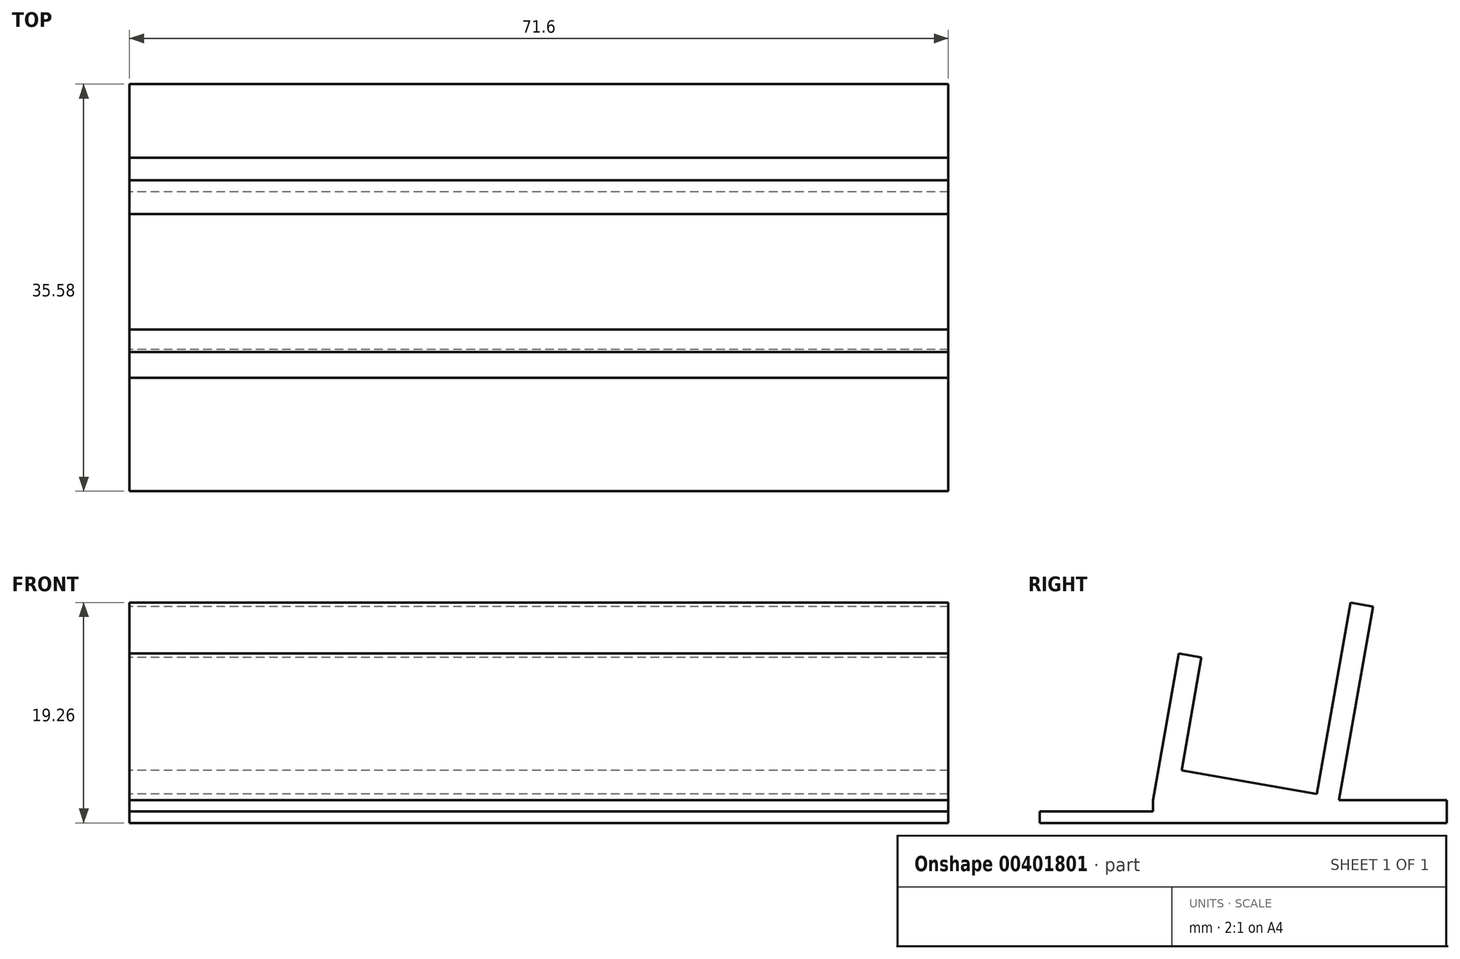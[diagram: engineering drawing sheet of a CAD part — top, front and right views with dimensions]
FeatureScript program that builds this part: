
annotation { "Feature Type Name" : "Feature", "Feature Type Description" : "" }
export const myFeature = defineFeature(function(context is Context, id is Id, definition is map)
    precondition{}
    {
        {
            var Q0;
            Q0=qCreatedBy(makeId("Right.planeOp"),FACE);
            var sketch = newSketch(context, id + "F0", { "sketchPlane" : qUnion([Q0])});
            skLineSegment(sketch, "E0", {"start": v(0, 0) * mm, "end": v(2.95, 16.74) * mm});
            skLineSegment(sketch, "E1", {"start": v(-11.82, 2.08) * mm, "end": v(0, 0) * mm});
            skLineSegment(sketch, "E2", {"start": v(-11.82, 2.08) * mm, "end": v(-10.08, 11.93) * mm});
            skLineSegment(sketch, "E3", {"start": v(0, 0) * mm, "end": v(8.95, 0) * mm, "construction": true});
            skLineSegment(sketch, "E4.0", {"start": v(-14.3, -0.52) * mm, "end": v(-12.05, 12.28) * mm});
            skLineSegment(sketch, "E4.2", {"start": v(1.94, -0.52) * mm, "end": v(4.92, 16.4) * mm});
            skLineSegment(sketch, "E5", {"start": v(-12.05, 12.28) * mm, "end": v(-10.08, 11.93) * mm});
            skLineSegment(sketch, "E6", {"start": v(2.95, 16.74) * mm, "end": v(4.92, 16.4) * mm});
            skLineSegment(sketch, "E7.bottom", {"start": v(11.37, -2.52) * mm, "end": v(-14.3, -2.52) * mm});
            skLineSegment(sketch, "E7.top", {"start": v(11.37, -0.52) * mm, "end": v(1.94, -0.52) * mm});
            skLineSegment(sketch, "E7.left", {"start": v(11.37, -2.52) * mm, "end": v(11.37, -0.52) * mm});
            skLineSegment(sketch, "E7.right", {"start": v(-14.3, -2.52) * mm, "end": v(-14.3, -0.52) * mm});
            skSolve(sketch);
        }
        {
            var Q0;
            Q0 = qSketchRegion(id + "F0", true);
            extrude(context, id + "F1", {"entities" : qUnion([Q0]), "endBound" : BoundingType.SYMMETRIC, "depth" : 71.6 * mm});
        }
        {
            var Q0;
            Q0=makeQuery(id+"F1.opExtrude","SWEPT_FACE",FACE,{"disambiguationData":[OSD([sQuery(id+"F0.wireOp",EDGE,"E7.right")])]});
            var sketch = newSketch(context, id + "F2", { "sketchPlane" : qUnion([Q0])});
            skLineSegment(sketch, "E8.bottom", {"start": v(-35.8, -2.52) * mm, "end": v(35.8, -2.52) * mm});
            skLineSegment(sketch, "E8.top", {"start": v(-35.8, -1.52) * mm, "end": v(35.8, -1.52) * mm});
            skLineSegment(sketch, "E8.left", {"start": v(-35.8, -2.52) * mm, "end": v(-35.8, -1.52) * mm});
            skLineSegment(sketch, "E8.right", {"start": v(35.8, -2.52) * mm, "end": v(35.8, -1.52) * mm});
            skSolve(sketch);
        }
        {
            var Q0;
            Q0 = qSketchRegion(id + "F2", true);
            extrude(context, id + "F3", {"entities" : qUnion([Q0]), "operationType" : NewBodyOperationType.ADD, "depth" : 9.9 * mm});
        }
    });
